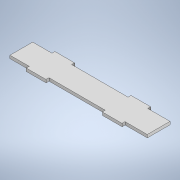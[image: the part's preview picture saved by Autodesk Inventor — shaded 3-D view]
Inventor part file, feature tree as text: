
AUTODESK INVENTOR PART (.ipt)
format: ipt  version: 2022 (Build 260153000, 153)  size: 123,904 bytes
history: native  units: in
note: dims shown in document units (in); Inventor stores cm internally (conversion verified against a paired STEP export)
features: extrude x1, sketch x1
ambient origin geometry x8: Origin, YZ Plane, XZ Plane, XY Plane, X Axis, Y Axis, Z Axis, Center Point
bodies: Solid1 (feature_tree)
feature tree (2):
  extrude  "Extrusion1"  Depth=0.1181in
  sketch  "Sketch1"  dims[d0=0.9055in d1=5.5906in d2=0.1181in d3=0.7874in d4=0.1181in d5=0.7874in d6=0.1181in d7=1.5157in d8=0.7874in d10=3.0315in d11=0.3937in d13=0.3937in d15=0.1181in d16=0.0in]
